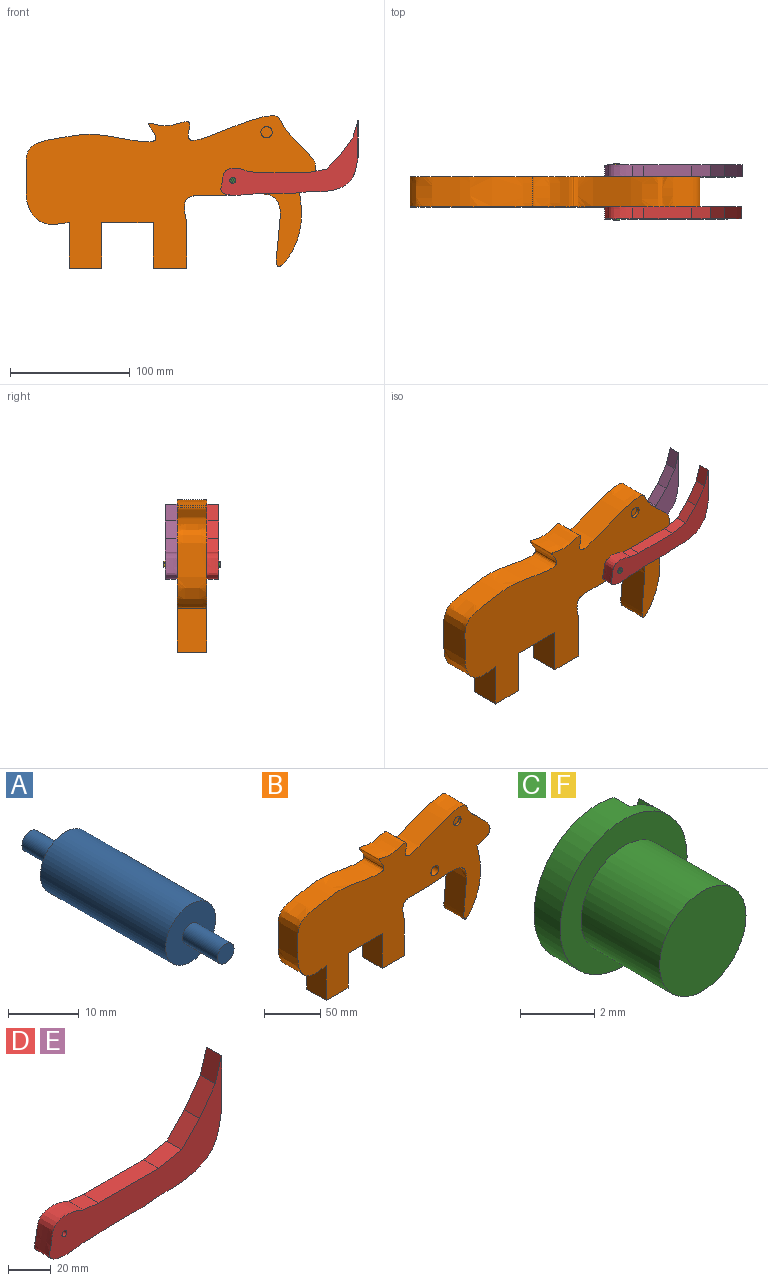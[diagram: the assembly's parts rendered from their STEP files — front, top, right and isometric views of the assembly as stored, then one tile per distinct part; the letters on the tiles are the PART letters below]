
ASSEMBLY  parts=6 mates=5
PART A: 7 faces, bbox 10x39x10 mm
  f0: cylinder r=5mm len=25mm, axis (0,1,0), area 785.4mm2, adj f1,f2
  f1: plane 10x10mm, normal (0,-1,0), area 70mm2, adj f0,f3
  f2: plane 10x10mm, normal (0,1,0), area 69.8mm2, adj f0,f5
  f3: cylinder r=1.65mm len=7mm, axis (0,1,0), area 72.6mm2, adj f1,f4
  f4: plane 3.3x3.3mm, normal (0,-1,0), area 8.6mm2, adj f3
  f5: cylinder r=1.67mm len=7mm, axis (0,-1,0), area 73.2mm2, adj f2,f6
  f6: plane 3.33x3.33mm, normal (0,1,0), area 8.7mm2, adj f5
PART B: 14 faces, bbox 249.4x25x131.8 mm
  f0: plane 38x25mm, normal (1,0,0), area 950mm2, adj f1,f8,f9,f10
  f1: extruded ~97.59x73.05mm, area 5858.9mm2, adj f0,f2,f9,f10
  f2: extruded ~241.43x90.36mm, area 10514.2mm2, adj f1,f3,f9,f10
  f3: plane 38x25mm, normal (-1,0,0), area 950mm2, adj f2,f4,f9,f10
  f4: plane 27.11x25mm, normal (0,0,-1), area 677.8mm2, adj f3,f5,f9,f10
  f5: plane 38x25mm, normal (1,0,0), area 950mm2, adj f4,f6,f9,f10
  f6: plane 42.95x25mm, normal (0,0,-1), area 1073.8mm2, adj f5,f7,f9,f10
  f7: plane 38x25mm, normal (-1,0,0), area 950mm2, adj f6,f8,f9,f10
  f8: plane 27.98x25mm, normal (0,0,-1), area 699.6mm2, adj f0,f7,f9,f10
  f9: plane 249.42x131.83mm, normal (0,-1,0), area 17954.6mm2, adj f0,f1,f2,f3,f4,f5,f6,f7
  f10: plane 249.42x131.83mm, normal (0,1,0), area 18024.2mm2, adj f0,f1,f2,f3,f4,f5,f6,f7
  f11: cylinder r=5mm len=25mm, axis (0,-1,0), area 785.4mm2, adj f9,f10
  f12: cylinder r=4.71mm len=9.41mm, axis (0,-1,0), area 73.9mm2, adj f9,f13
  f13: plane 9.41x9.41mm, normal (0,-1,0), area 69.6mm2, adj f12
PART C: 9 faces, bbox 4.8x4x4.8 mm
  f0: plane 4.25x2.89mm, normal (0,1,0), area 6.2mm2, adj f3,f6
  f1: cylinder r=1.65mm len=3.3mm, axis (0,1,0), area 31.1mm2, adj f2,f4
  f2: plane 3.3x3.3mm, normal (0,-1,0), area 8.6mm2, adj f1
  f3: cylinder r=2.42mm len=4.85mm, axis (0,1,0), area 13.8mm2, adj f0,f4,f5,f6,f7,f8
  f4: plane 4.85x4.85mm, normal (0,-1,0), area 9.9mm2, adj f1,f3
  f5: plane 4.28x3.06mm, normal (0,1,0), area 6.7mm2, adj f3,f7
  f6: plane 4.2x2.06mm, normal (-0.9,0,0.44), area 2.8mm2, adj f0,f3,f8
  f7: plane 4.19x2.2mm, normal (0.89,0,-0.46), area 2.8mm2, adj f3,f5,f8
  f8: plane 4.72x3.16mm, normal (0,1,0), area 5.5mm2, adj f3,f6,f7
PART D: 15 faces, bbox 114.6x10x63.2 mm
  f0: plane 10x9.64mm, normal (0.09,0,1), area 96.7mm2, adj f1,f11,f12,f13
  f1: extruded ~22.82x22.71mm, area 593.5mm2, adj f0,f2,f12,f13
  f2: extruded ~18.26x10mm, area 183.4mm2, adj f1,f3,f12,f13
  f3: plane 22.51x10mm, normal (0,0,-1), area 225.1mm2, adj f2,f4,f12,f13
  f4: extruded ~52.15x29.37mm, area 686.3mm2, adj f3,f5,f12,f13
  f5: plane 17.41x10mm, normal (1,0,0), area 174.1mm2, adj f4,f6,f12,f13
  f6: plane 14.16x10mm, normal (1,0,0), area 141.6mm2, adj f5,f7,f12,f13
  f7: plane 14.16x10mm, normal (-0.96,0,0.28), area 147.5mm2, adj f6,f8,f12,f13
  f8: plane 14.69x10.44mm, normal (-0.81,0,0.58), area 180.2mm2, adj f7,f9,f12,f13
  f9: plane 12.08x11.75mm, normal (-0.72,0,0.7), area 168.5mm2, adj f8,f10,f12,f13
  f10: plane 15.67x10mm, normal (-0.18,0,0.98), area 159.4mm2, adj f9,f11,f12,f13
  f11: plane 39.89x10mm, normal (0,0,1), area 398.9mm2, adj f0,f10,f12,f13
  f12: plane 114.59x63.23mm, normal (0,1,0), area 2315.9mm2, adj f0,f1,f2,f3,f4,f5,f6,f7
  f13: plane 114.59x63.23mm, normal (0,-1,0), area 2315.9mm2, adj f0,f1,f2,f3,f4,f5,f6,f7
  f14: cylinder r=1.65mm len=10mm, axis (0,-1,0), area 103.7mm2, adj f12,f13
PART E: same geometry as D
PART F: same geometry as C
PLACE A t=(92.1,74.82,6.17)mm
PLACE B t=(1.65,74.82,-2.07)mm
PLACE C rot(axis=(1,0,0),180deg) t=(77.1,38.82,63.17)mm
PLACE D t=(77.49,39.82,-6.98)mm
PLACE E t=(77.49,74.82,-6.98)mm
PLACE F rot(axis=(0,-1,0),90deg) t=(67.65,85.82,72.62)mm
MATE slider D.f14 <-> B.f11  axis (0,1,0) through (44.55,49.82,40.07)mm
MATE slider E.f14 <-> A.f0  axis (0,-1,0) through (44.55,84.82,40.07)mm
MATE cylindrical A.f0 <-> B.f11  axis (0,-1,0) through (44.55,42.82,40.07)mm
MATE cylindrical F.f1 <-> A.f0  axis (0,-1,0) through (44.55,81.82,40.07)mm
MATE cylindrical C.f1 <-> D.f14  axis (0,1,0) through (44.55,42.82,40.07)mm
